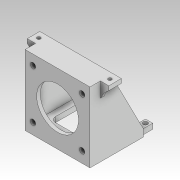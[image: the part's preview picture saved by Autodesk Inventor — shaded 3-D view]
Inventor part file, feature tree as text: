
AUTODESK INVENTOR PART (.ipt)
format: ipt  version: 2020 (Build 240168000, 168)  size: 316,928 bytes
history: native  units: mm
features: extrude x11, sketch x11, fillet x4, projected_geometry x3, mirror x2, plane x1, chamfer x1
ambient origin geometry x8: Origin, YZ Plane, XZ Plane, XY Plane, X Axis, Y Axis, Z Axis, Center Point
bodies: Solid1 (feature_tree)
feature tree (33):
  extrude  "Extrusion1"  Depth=47.0mm
  extrude  "Extrusion2"  Depth=40.0mm
  extrude  "Extrusion3"  Depth=3.5mm TaperAngle=0.0deg
  extrude  "Extrusion4"  Depth=12.0mm
  mirror  "Mirror1"
  fillet  "Fillet1"  Radius=4.0mm
  extrude  "Extrusion5"  TaperAngle=0.0deg  [1 undecoded]
  plane  "Work Plane1"
  extrude  "Extrusion6"  Depth=25.0mm
  extrude  "Extrusion7"  Depth=5.0mm
  extrude  "Extrusion8"  TaperAngle=0.0deg  [1 undecoded]
  extrude  "Extrusion9"  Depth=10.0mm TaperAngle=0.0deg
  chamfer  "Chamfer2"  Distance=6.0mm
  mirror  "Mirror2"
  extrude  "Extrusion10"  Depth=10.0mm
  extrude  "Extrusion11"  Depth=10.0mm
  fillet  "Fillet2"  Radius=5.0mm
  fillet  "Fillet3"  Radius=44.8mm
  fillet  "Fillet4"  Radius=5.0mm
  sketch  "Sketch1"  dims[d0=5.2mm d1=47.0mm]
  sketch  "Sketch2"  dims[d2=47.0mm d3=40.0mm]
  projected_geometry  "Projected Loop1"
  sketch  "Sketch3"  dims[d4=58.0mm d5=3.5mm d6=0.0mm]
  sketch  "Sketch4"  dims[d7=10.0mm d8=12.0mm d9=4.0mm d10=0.0mm]
  sketch  "Sketch5"  dims[d15=4.0mm d16=0.0mm d18=0.0mm d19=0.0mm]
  sketch  "Sketch6"  dims[d20=45.0deg d21=25.0mm]
  sketch  "Sketch7"  dims[d22=5.0mm d23=5.0mm]
  sketch  "Sketch8"  dims[d24=3.3mm d25=0.0mm d26=0.0mm]
  sketch  "Sketch9"  dims[d27=6.0mm d28=10.0mm d29=0.0mm]
  sketch  "Sketch10"  dims[d30=-6.5mm]
  projected_geometry  "Projected Loop2"
  sketch  "Sketch11"  dims[d32=6.0mm d33=6.0mm d35=7.2mm d36=7.0mm d37=5.0mm d38=0.0mm d39=44.8mm d40=5.0mm d41=6.0mm d42=3.5mm d43=4.3mm d44=5.0mm d45=0.0mm d46=2.0mm d47=2.0mm d50=2.0mm d51=0.0mm d52=1.0mm d53=2.0mm d54=45.0deg d55=2.0mm d56=42.0mm d57=10.0mm d58=0.0mm d59=10.0mm d60=0.0mm]
  projected_geometry  "Projected Loop3"
note: 2 required parameter values undecoded (feature->parameter linkage not recoverable at this tier; creation-order binding heuristic only, values carry confidence <= 0.55)
